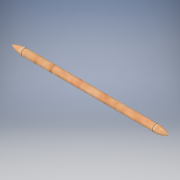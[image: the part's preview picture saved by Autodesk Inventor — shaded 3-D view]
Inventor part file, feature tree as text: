
AUTODESK INVENTOR PART (.ipt)
format: ipt  version: 2016 (Build 200138000, 138)  size: 107,008 bytes
history: native  units: in
note: dims shown in document units (in); Inventor stores cm internally (conversion verified against a paired STEP export)
features: sketch x2, extrude x1, revolve x1
ambient origin geometry x8: Origin, YZ Plane, XZ Plane, XY Plane, X Axis, Y Axis, Z Axis, Center Point
bodies: Solid1 (feature_tree)
feature tree (4):
  extrude  "Extrusion1"  Depth=2.0in TaperAngle=0.0deg
  revolve  "Revolution1"  [1 undecoded]
  sketch  "Sketch1"  dims[d0=0.1in d1=2.0in d2=0.0in]
  sketch  "Sketch2"  dims[d3=0.2in d4=0.2in d5=90.0deg]
note: 1 required parameter value undecoded (feature->parameter linkage not recoverable at this tier; creation-order binding heuristic only, values carry confidence <= 0.55)
